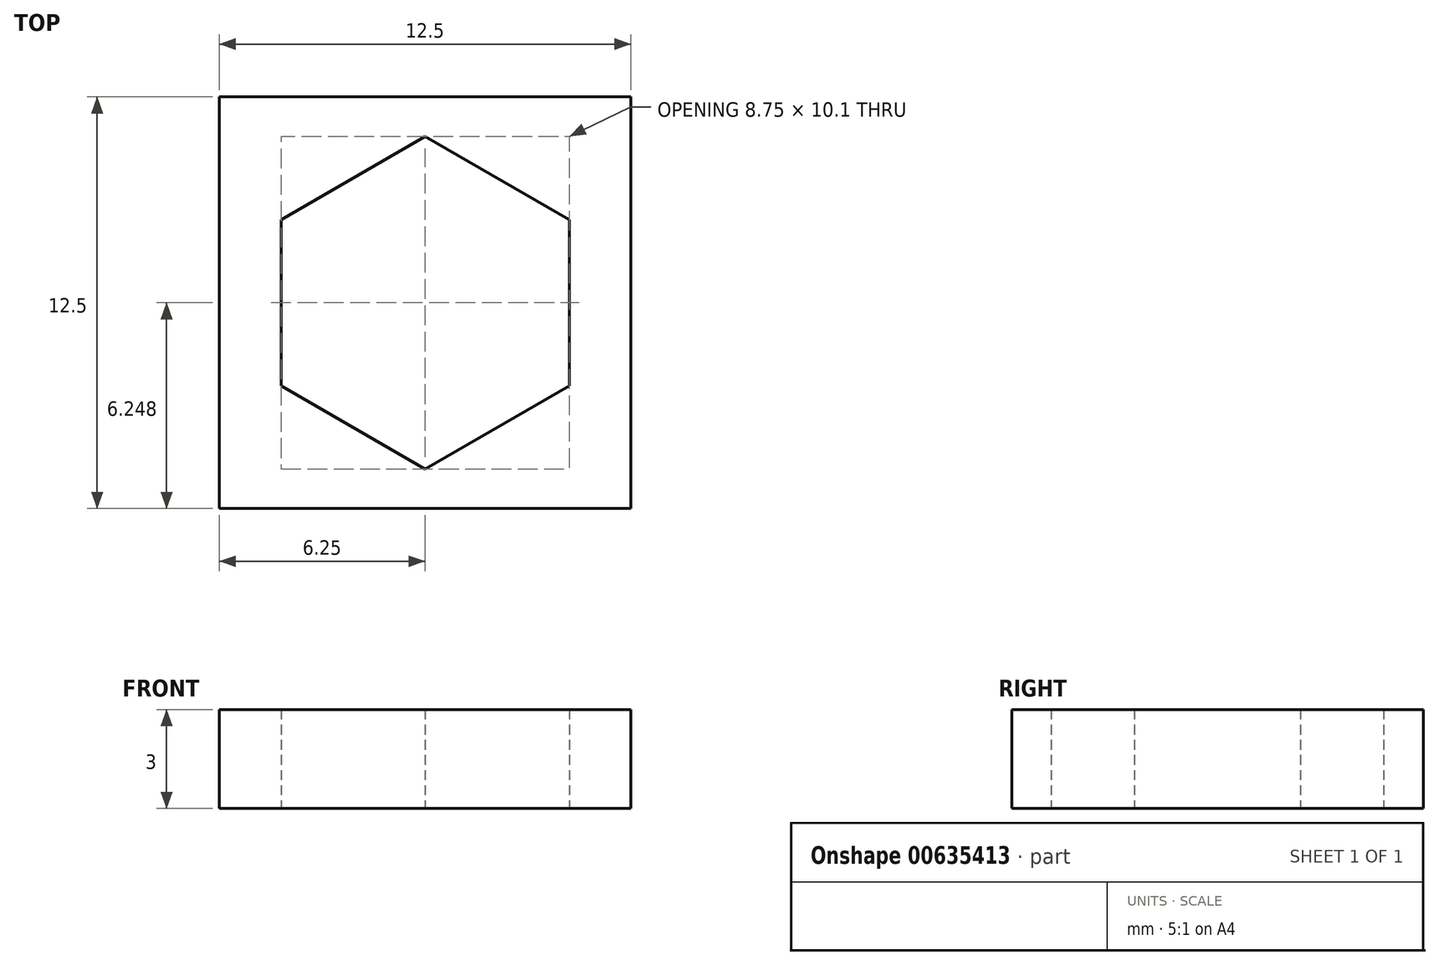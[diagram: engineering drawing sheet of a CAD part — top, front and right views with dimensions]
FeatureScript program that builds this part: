
annotation { "Feature Type Name" : "Feature", "Feature Type Description" : "" }
export const myFeature = defineFeature(function(context is Context, id is Id, definition is map)
    precondition{}
    {
        {
            var Q0;
            Q0=qCreatedBy(makeId("Top.planeOp"),FACE);
            var sketch = newSketch(context, id + "F0", { "sketchPlane" : qUnion([Q0])});
            skLineSegment(sketch, "E0.bottom", {"start": v(0, 0) * mm, "end": v(12.5, 0) * mm});
            skLineSegment(sketch, "E0.top", {"start": v(0, 12.5) * mm, "end": v(12.5, 12.5) * mm});
            skLineSegment(sketch, "E0.left", {"start": v(0, 0) * mm, "end": v(0, 12.5) * mm});
            skLineSegment(sketch, "E0.right", {"start": v(12.5, 0) * mm, "end": v(12.5, 12.5) * mm});
            skCircle(sketch, "E1.cCircle", {"center": v(6.25, 6.25) * mm, "radius": 4.38 * mm, "construction": true});
            skPoint(sketch, "E1.cCircle.centerSnap0", {"position": v(0, 6.25) * mm});
            skPoint(sketch, "E1.cCircle.centerSnap1", {"position": v(6.25, 0) * mm});
            skLineSegment(sketch, "E1.0", {"start": v(10.62, 8.77) * mm, "end": v(10.62, 3.72) * mm});
            skLineSegment(sketch, "E1.1", {"start": v(10.62, 3.72) * mm, "end": v(6.25, 1.2) * mm});
            skLineSegment(sketch, "E1.2", {"start": v(6.25, 1.2) * mm, "end": v(1.88, 3.72) * mm});
            skLineSegment(sketch, "E1.3", {"start": v(1.88, 3.72) * mm, "end": v(1.87, 8.77) * mm});
            skLineSegment(sketch, "E1.4", {"start": v(1.87, 8.77) * mm, "end": v(6.25, 11.3) * mm});
            skLineSegment(sketch, "E1.5", {"start": v(6.25, 11.3) * mm, "end": v(10.62, 8.77) * mm});
            skPoint(sketch, "E1.0.midPoint", {"position": v(10.62, 6.25) * mm});
            skSolve(sketch);
        }
        {
            var Q0;
            Q0=makeQuery(id+"F0.imprint","IMPRINT",FACE,{"disambiguationData":[TD([[makeQuery(id+"F0.imprint","IMPRINT",EDGE,{"derivedFrom":sQuery(id+"F0.wireOp",EDGE,"E0.bottom")}),1.0]])]});
            extrude(context, id + "F1", {"entities" : qUnion([Q0]), "depth" : 3 * mm, "offsetDistance" : 25.4 * mm});
        }
    });
